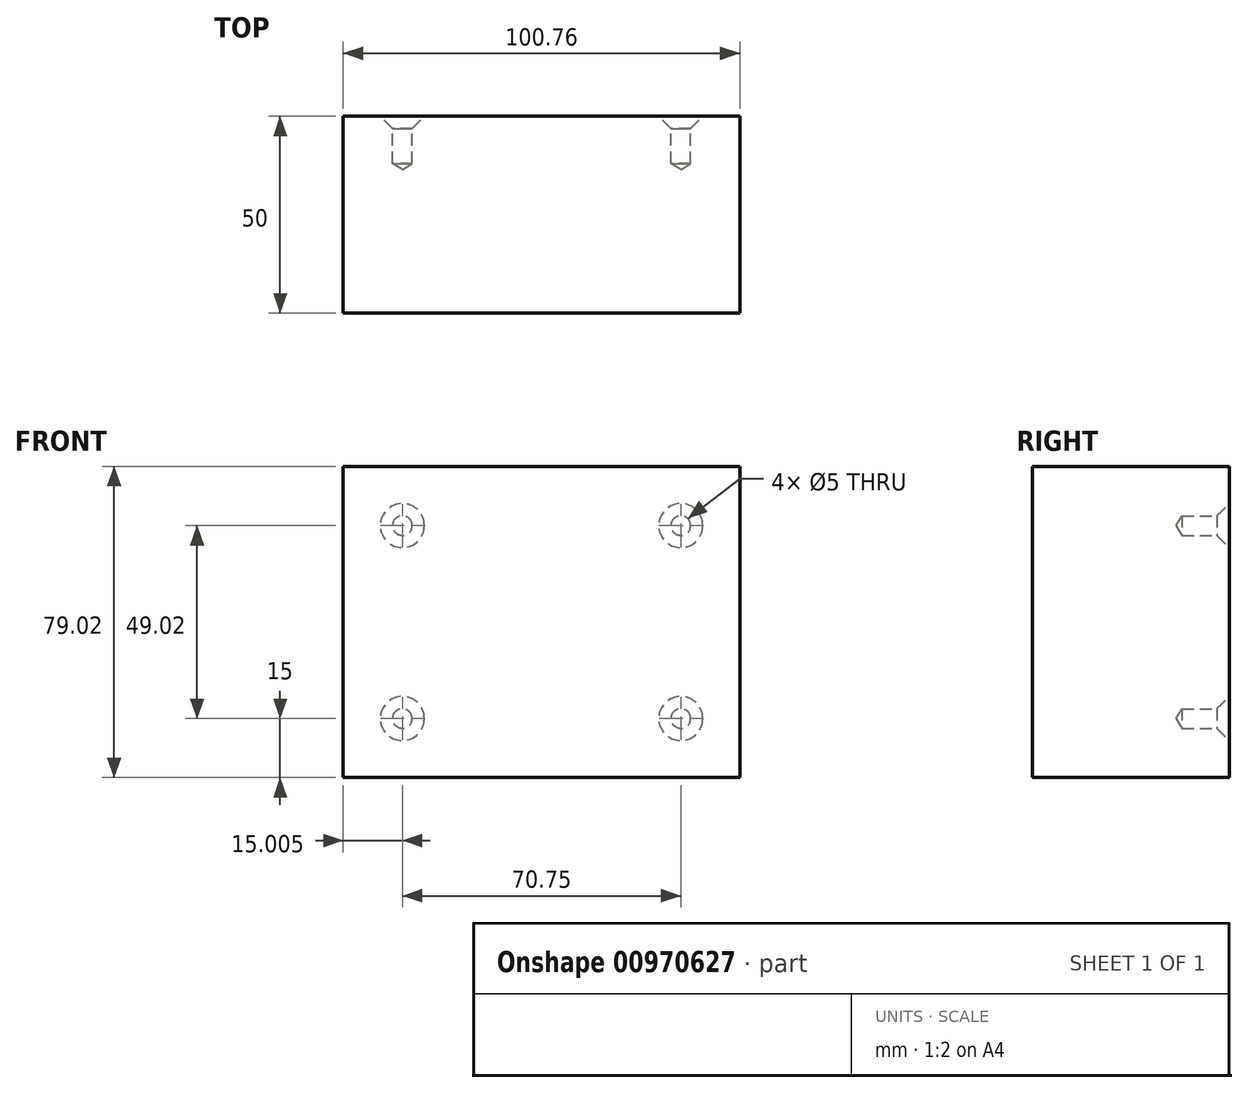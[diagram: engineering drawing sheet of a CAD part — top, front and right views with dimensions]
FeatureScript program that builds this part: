
annotation { "Feature Type Name" : "Feature", "Feature Type Description" : "" }
export const myFeature = defineFeature(function(context is Context, id is Id, definition is map)
    precondition{}
    {
        {
            var Q0;
            Q0=qCreatedBy(makeId("Front.planeOp"),FACE);
            var sketch = newSketch(context, id + "F0", { "sketchPlane" : qUnion([Q0])});
            skLineSegment(sketch, "E0.bottom", {"start": v(50.38, -39.5) * mm, "end": v(-50.38, -39.5) * mm});
            skLineSegment(sketch, "E0.top", {"start": v(50.38, 39.5) * mm, "end": v(-50.38, 39.5) * mm});
            skLineSegment(sketch, "E0.left", {"start": v(50.38, -39.5) * mm, "end": v(50.38, 39.5) * mm});
            skLineSegment(sketch, "E0.right", {"start": v(-50.38, -39.5) * mm, "end": v(-50.38, 39.5) * mm});
            skPoint(sketch, "E0.middle", {"position": v(0, 0) * mm});
            skLineSegment(sketch, "E1.0", {"start": v(35.38, 24.5) * mm, "end": v(-35.38, 24.5) * mm, "construction": true});
            skLineSegment(sketch, "E1.1", {"start": v(35.38, -24.5) * mm, "end": v(35.38, 24.5) * mm, "construction": true});
            skLineSegment(sketch, "E1.2", {"start": v(35.38, -24.5) * mm, "end": v(-35.38, -24.5) * mm, "construction": true});
            skLineSegment(sketch, "E1.3", {"start": v(-35.38, -24.5) * mm, "end": v(-35.38, 24.5) * mm, "construction": true});
            skPoint(sketch, "E2", {"position": v(-35.38, 24.5) * mm});
            skPoint(sketch, "E3", {"position": v(35.38, 24.5) * mm});
            skPoint(sketch, "E4", {"position": v(-35.38, -24.5) * mm});
            skPoint(sketch, "E5", {"position": v(35.38, -24.5) * mm});
            skSolve(sketch);
        }
        {
            var Q0;
            Q0=makeQuery(id+"F0.imprint","IMPRINT",FACE,{"disambiguationData":[TD([[makeQuery(id+"F0.imprint","IMPRINT",EDGE,{"derivedFrom":sQuery(id+"F0.wireOp",EDGE,"E0.bottom")}),-1.0]])]});
            extrude(context, id + "F1", {"entities" : qUnion([Q0]), "depth" : 50 * mm, "offsetDistance" : 25 * mm});
        }
        {
            var Q0;
            Q0=sQuery(id+"F0.wireOp",VERTEX,"E2");
            var Q1;
            Q1=sQuery(id+"F0.wireOp",VERTEX,"E3");
            var Q2;
            Q2=sQuery(id+"F0.wireOp",VERTEX,"E5");
            var Q3;
            Q3=sQuery(id+"F0.wireOp",VERTEX,"E4");
            var Q4;
            Q4=makeQuery(id+"F1.opExtrude","SWEPT_BODY",BODY,{"disambiguationData":[OSD([sQuery(id+"F0.wireOp",EDGE,"E0.bottom"),sQuery(id+"F0.wireOp",EDGE,"E0.top"),sQuery(id+"F0.wireOp",EDGE,"E0.left"),sQuery(id+"F0.wireOp",EDGE,"E0.right")])]});
            hole(context, id + "F2", {"style" : HoleStyle.C_SINK, "endStyle" : HoleEndStyle.BLIND, "oppositeDirection" : true, "standardTappedOrClearance" : lookupTablePath({ "standard" : "ISO", "size" : "5", "type" : "Drilled" }), "standardBlindInLast" : lookupTablePath({ "standard" : "ISO", "size" : "5", "type" : "Drilled" }), "holeDiameter" : 5 * mm, "cSinkDiameter" : 11.2 * mm, "cSinkAngle" : 90 * degree, "majorDiameter" : 5 * mm, "holeDepth" : 12 * mm, "isTappedThrough" : true, "tappedDepth" : 12 * mm, "tapClearance" : 3, "locations" : qUnion([Q0, Q1, Q2, Q3]), "scope" : qUnion([Q4])});
        }
    });
